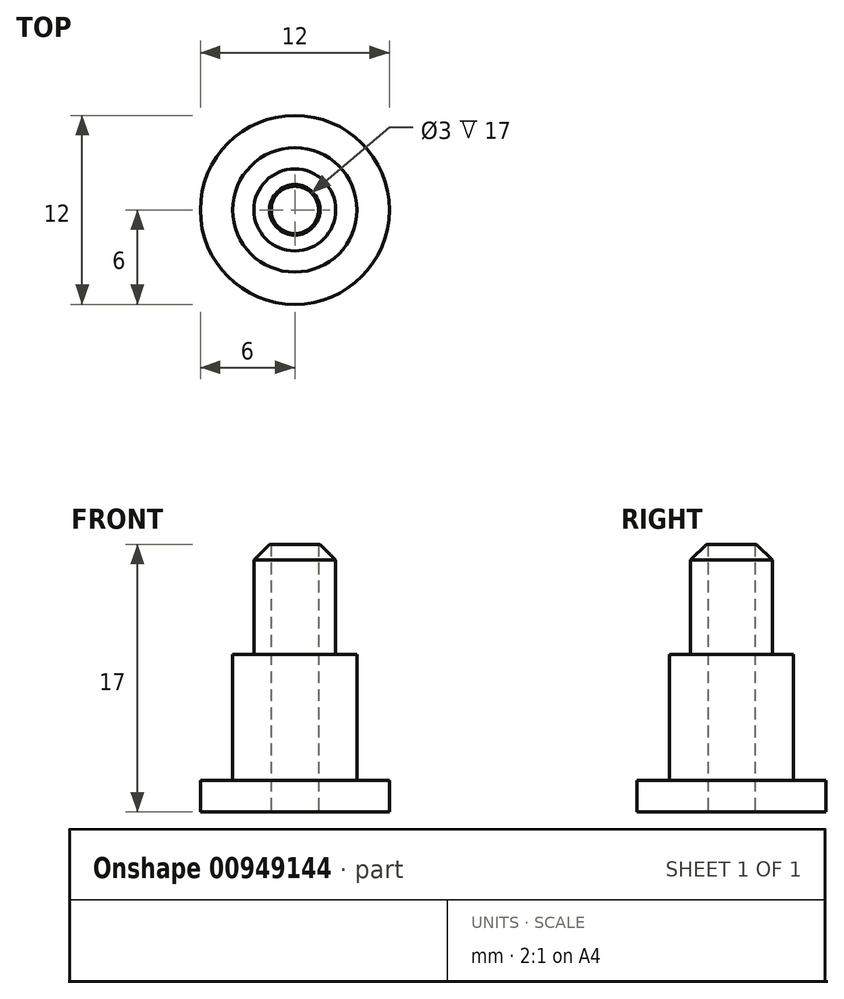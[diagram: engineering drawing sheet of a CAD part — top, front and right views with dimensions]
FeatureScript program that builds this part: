
annotation { "Feature Type Name" : "Feature", "Feature Type Description" : "" }
export const myFeature = defineFeature(function(context is Context, id is Id, definition is map)
    precondition{}
    {
        {
            var Q0;
            Q0=qCreatedBy(makeId("Top.planeOp"),FACE);
            var sketch = newSketch(context, id + "F0", { "sketchPlane" : qUnion([Q0])});
            skCircle(sketch, "E0", {"center": v(0, 0) * mm, "radius": 3.95 * mm});
            skSolve(sketch);
        }
        {
            var Q0;
            Q0 = qSketchRegion(id + "F0", true);
            extrude(context, id + "F1", {"entities" : qUnion([Q0]), "depth" : 8 * mm, "offsetDistance" : 25.4 * mm});
        }
        {
            var Q0;
            Q0=makeQuery(id+"F1.opExtrude","CAP_FACE",FACE,{"disambiguationData":[OSD([sQuery(id+"F0.wireOp",EDGE,"E0")])],"isStart":false});
            var sketch = newSketch(context, id + "F2", { "sketchPlane" : qUnion([Q0])});
            skCircle(sketch, "E1", {"center": v(0, 0) * mm, "radius": 2.6 * mm});
            skSolve(sketch);
        }
        {
            var Q0;
            Q0 = qSketchRegion(id + "F2", true);
            extrude(context, id + "F3", {"entities" : qUnion([Q0]), "operationType" : NewBodyOperationType.ADD, "depth" : 7 * mm, "offsetDistance" : 25.4 * mm});
        }
        {
            var Q0;
            Q0=makeQuery(id+"F3.opExtrude","CAP_EDGE",EDGE,{"disambiguationData":[OSD([sQuery(id+"F2.wireOp",EDGE,"E1")])],"isStart":false});
            chamfer(context, id + "F4", {"entities" : qUnion([Q0]), "width" : 1 * mm, "tangentPropagation" : true});
        }
        {
            var Q0;
            Q0=makeQuery(id+"F1.opExtrude","CAP_FACE",FACE,{"disambiguationData":[OSD([sQuery(id+"F0.wireOp",EDGE,"E0")])],"isStart":true});
            var sketch = newSketch(context, id + "F5", { "sketchPlane" : qUnion([Q0])});
            skCircle(sketch, "E2", {"center": v(0, 0) * mm, "radius": 6 * mm});
            skSolve(sketch);
        }
        {
            var Q0;
            Q0 = qSketchRegion(id + "F5", true);
            extrude(context, id + "F6", {"entities" : qUnion([Q0]), "operationType" : NewBodyOperationType.ADD, "depth" : 2 * mm, "offsetDistance" : 25.4 * mm});
        }
        {
            var Q0;
            Q0=makeQuery(id+"F6.opExtrude","CAP_FACE",FACE,{"disambiguationData":[OSD([sQuery(id+"F5.wireOp",EDGE,"E2")])],"isStart":false});
            var sketch = newSketch(context, id + "F7", { "sketchPlane" : qUnion([Q0])});
            skCircle(sketch, "E3", {"center": v(0, 0) * mm, "radius": 1.5 * mm});
            skSolve(sketch);
        }
        {
            var Q0;
            Q0 = qSketchRegion(id + "F7", true);
            extrude(context, id + "F8", {"entities" : qUnion([Q0]), "operationType" : NewBodyOperationType.REMOVE, "endBound" : BoundingType.THROUGH_ALL, "oppositeDirection" : true, "depth" : 25.4 * mm, "offsetDistance" : 25.4 * mm});
        }
    });
